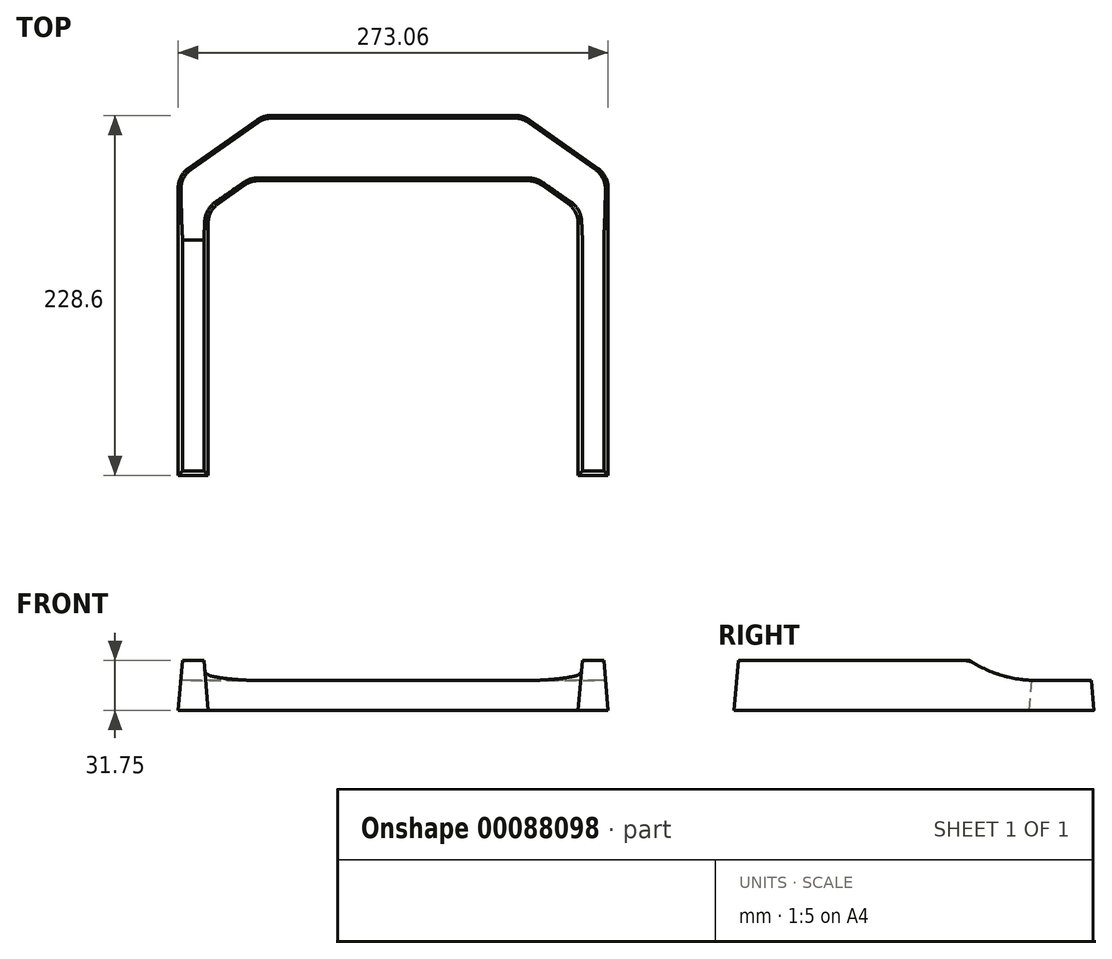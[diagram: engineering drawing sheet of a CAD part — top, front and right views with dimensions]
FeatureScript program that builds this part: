
annotation { "Feature Type Name" : "Feature", "Feature Type Description" : "" }
export const myFeature = defineFeature(function(context is Context, id is Id, definition is map)
    precondition{}
    {
        {
            var Q0;
            Q0=qCreatedBy(makeId("Top.planeOp"),FACE);
            var sketch = newSketch(context, id + "F0", { "sketchPlane" : qUnion([Q0])});
            skLineSegment(sketch, "E0", {"start": v(-136.53, 0) * mm, "end": v(-136.53, 190.5) * mm});
            skLineSegment(sketch, "E1", {"start": v(-136.53, 190.5) * mm, "end": v(-82.55, 228.6) * mm});
            skLineSegment(sketch, "E2", {"start": v(-82.55, 228.6) * mm, "end": v(82.55, 228.6) * mm});
            skLineSegment(sketch, "E3", {"start": v(82.55, 228.6) * mm, "end": v(136.53, 190.5) * mm});
            skLineSegment(sketch, "E4", {"start": v(136.52, 190.5) * mm, "end": v(136.53, 0) * mm});
            skLineSegment(sketch, "E5", {"start": v(136.53, 0) * mm, "end": v(117.48, 0) * mm});
            skLineSegment(sketch, "E6", {"start": v(117.48, 0) * mm, "end": v(117.48, 168.15) * mm});
            skLineSegment(sketch, "E7", {"start": v(117.48, 168.15) * mm, "end": v(90.49, 187.2) * mm});
            skLineSegment(sketch, "E8", {"start": v(90.49, 187.2) * mm, "end": v(-90.49, 187.2) * mm});
            skLineSegment(sketch, "E9", {"start": v(-90.49, 187.2) * mm, "end": v(-117.48, 168.15) * mm});
            skLineSegment(sketch, "E10", {"start": v(-117.48, 168.15) * mm, "end": v(-117.48, 0) * mm});
            skLineSegment(sketch, "E11", {"start": v(-117.48, 0) * mm, "end": v(-136.53, 0) * mm});
            skLineSegment(sketch, "E12", {"start": v(0, 0) * mm, "end": v(0, 111.72) * mm, "construction": true});
            skPoint(sketch, "E12.endSnap0", {"position": v(0, 187.2) * mm});
            skSolve(sketch);
        }
        {
            var Q0;
            Q0 = qSketchRegion(id + "F0", true);
            extrude(context, id + "F1", {"entities" : qUnion([Q0]), "depth" : 31.75 * mm, "hasDraft" : true, "draftAngle" : 5 * degree, "draftPullDirection" : true});
        }
        {
            var Q0;
            Q0=qCreatedBy(makeId("Right.planeOp"),FACE);
            var sketch = newSketch(context, id + "F2", { "sketchPlane" : qUnion([Q0])});
            skArc(sketch, "E13", {"start": v(149.62, 31.75) * mm, "mid": v(169.75, 22.3) * mm, "end": v(191.74, 19.05) * mm});
            skLineSegment(sketch, "E14", {"start": v(191.74, 19.05) * mm, "end": v(226.93, 19.05) * mm});
            skLineSegment(sketch, "E15", {"start": v(149.62, 31.75) * mm, "end": v(225.82, 31.75) * mm});
            skLineSegment(sketch, "E16", {"start": v(225.82, 31.75) * mm, "end": v(226.93, 19.05) * mm});
            skSolve(sketch);
        }
        {
            var Q0;
            Q0=makeQuery(id+"F2.imprint","IMPRINT",FACE,{"disambiguationData":[TD([[makeQuery(id+"F2.imprint","IMPRINT",EDGE,{"derivedFrom":sQuery(id+"F2.wireOp",EDGE,"E13")}),1.0]])]});
            extrude(context, id + "F3", {"entities" : qUnion([Q0]), "operationType" : NewBodyOperationType.REMOVE, "endBound" : BoundingType.THROUGH_ALL, "depth" : 25.4 * mm, "hasSecondDirection" : true, "secondDirectionBound" : SecondDirectionBoundingType.THROUGH_ALL, "secondDirectionOppositeDirection" : true, "secondDirectionDepth" : 25.4 * mm});
        }
        {
            var Q0;
            Q0=makeQuery(id+"F3.boolean.opBoolean","COPY",EDGE,{"disambiguationData":[OD(1.0)],"derivedFrom":makeQuery(id+"F3.opExtrude","SWEPT_EDGE",EDGE,{"disambiguationData":[OSD([sQuery(id+"F2.wireOp",EDGE,"E13"),sQuery(id+"F2.wireOp",EDGE,"E15")])]})});
            var Q1;
            Q1=makeQuery(id+"F3.boolean.opBoolean","COPY",EDGE,{"disambiguationData":[OD(0.0)],"derivedFrom":makeQuery(id+"F3.opExtrude","SWEPT_EDGE",EDGE,{"disambiguationData":[OSD([sQuery(id+"F2.wireOp",EDGE,"E13"),sQuery(id+"F2.wireOp",EDGE,"E15")])]})});
            var Q2;
            Q2=makeQuery(id+"F1.opExtrude","SWEPT_EDGE",EDGE,{"disambiguationData":[OSD([sQuery(id+"F0.wireOp",EDGE,"E3"),sQuery(id+"F0.wireOp",EDGE,"E4")])]});
            var Q3;
            Q3=makeQuery(id+"F1.opExtrude","SWEPT_EDGE",EDGE,{"disambiguationData":[OSD([sQuery(id+"F0.wireOp",EDGE,"E2"),sQuery(id+"F0.wireOp",EDGE,"E3")])]});
            var Q4;
            Q4=makeQuery(id+"F1.opExtrude","SWEPT_EDGE",EDGE,{"disambiguationData":[OSD([sQuery(id+"F0.wireOp",EDGE,"E1"),sQuery(id+"F0.wireOp",EDGE,"E2")])]});
            var Q5;
            Q5=makeQuery(id+"F1.opExtrude","SWEPT_EDGE",EDGE,{"disambiguationData":[OSD([sQuery(id+"F0.wireOp",EDGE,"E0"),sQuery(id+"F0.wireOp",EDGE,"E1")])]});
            var Q6;
            Q6=makeQuery(id+"F1.opExtrude","SWEPT_EDGE",EDGE,{"disambiguationData":[OSD([sQuery(id+"F0.wireOp",EDGE,"E8"),sQuery(id+"F0.wireOp",EDGE,"E9")])]});
            var Q7;
            Q7=makeQuery(id+"F1.opExtrude","SWEPT_EDGE",EDGE,{"disambiguationData":[OSD([sQuery(id+"F0.wireOp",EDGE,"E9"),sQuery(id+"F0.wireOp",EDGE,"E10")])]});
            var Q8;
            Q8=makeQuery(id+"F1.opExtrude","SWEPT_EDGE",EDGE,{"disambiguationData":[OSD([sQuery(id+"F0.wireOp",EDGE,"E7"),sQuery(id+"F0.wireOp",EDGE,"E8")])]});
            var Q9;
            Q9=makeQuery(id+"F1.opExtrude","SWEPT_EDGE",EDGE,{"disambiguationData":[OSD([sQuery(id+"F0.wireOp",EDGE,"E6"),sQuery(id+"F0.wireOp",EDGE,"E7")])]});
            fillet(context, id + "F4", {"entities" : qUnion([Q0, Q1, Q2, Q3, Q4, Q5, Q6, Q7, Q8, Q9]), "radius" : 15.24 * mm, "tangentPropagation" : true, "allowEdgeOverflow" : false});
        }
    });
